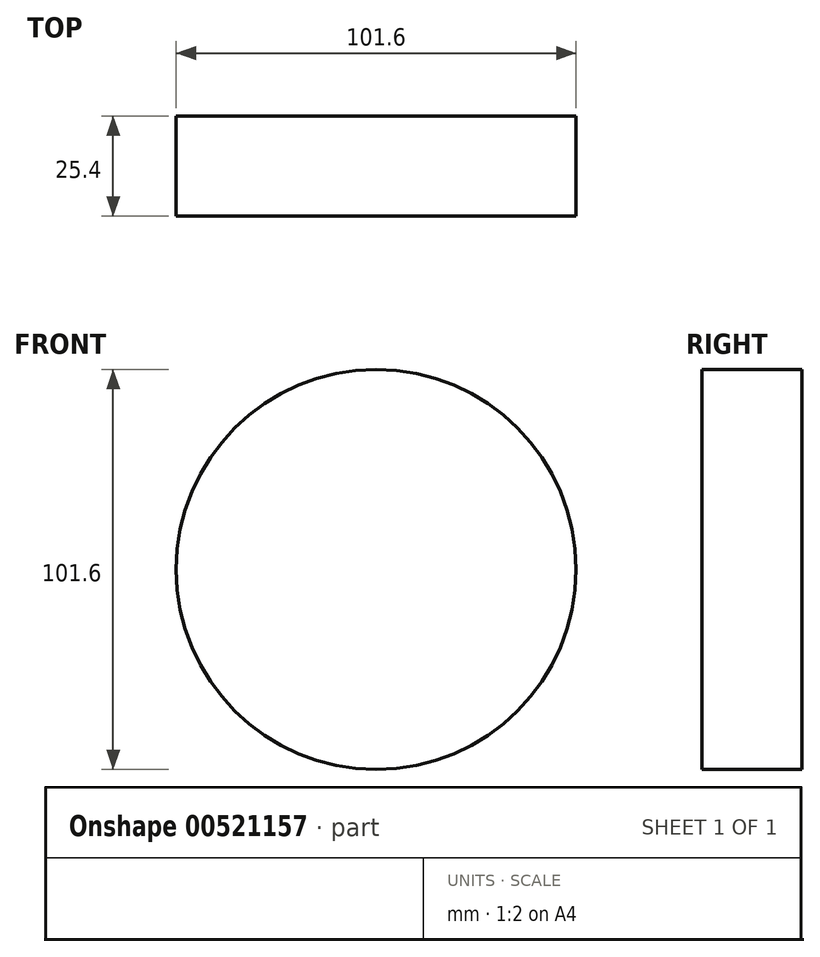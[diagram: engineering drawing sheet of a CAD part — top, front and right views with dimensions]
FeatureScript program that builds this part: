
annotation { "Feature Type Name" : "Feature", "Feature Type Description" : "" }
export const myFeature = defineFeature(function(context is Context, id is Id, definition is map)
    precondition{}
    {
        {
            var Q0;
            Q0=qCreatedBy(makeId("Front.planeOp"),FACE);
            var sketch = newSketch(context, id + "F0", { "sketchPlane" : qUnion([Q0])});
            skCircle(sketch, "E0", {"center": v(0, 0) * mm, "radius": 50.8 * mm});
            skSolve(sketch);
        }
        {
            var Q0;
            Q0=makeQuery(id+"F0.imprint","IMPRINT",FACE,{"disambiguationData":[TD([[makeQuery(id+"F0.imprint","IMPRINT",EDGE,{"derivedFrom":sQuery(id+"F0.wireOp",EDGE,"E0")}),1.0]])]});
            extrude(context, id + "F1", {"entities" : qUnion([Q0]), "depth" : 25.4 * mm, "offsetDistance" : 25.4 * mm});
        }
    });
